# Revit family: Washfountain_Lavatory-Bradley_Corp-WF2808-Type_O_Drain
name_source: partatom
category: Plumbing Fixtures
revit_build: Autodesk Revit MEP 2012 (Build: 20110309_2315(x64)
units: mm (PartAtom-declared; Revit-internal decimal feet)

## types (1)
- Washfountain_Lavatory-Bradley_Corp-WF2808-Type_O_Drain
    ADA Compliant = Yes
    Assembly Code = D2010300
    Buy American Act = No
    CWFU = 0
    Cold Lavatory Inlet = 1/2"
    Cold Lavatory Inlet Radius = 1/4"
    Description = Washfountain, 54" Circular with 9" Deep Bowl
    Drain = 2"
    Drain Radius = 1"
    Flow Rate = 5.0 gal/min
    Frequency = 50 Hz
    HWFU = 0
    Hot Lavatory Inlet = 1/2"
    Hot Lavatory Inlet Radius = 1/4"
    Industry Standards = ANSI Z124.3, Z124.6 and ANSI/ICPA SS-1-2001
    Manufacturer = Bradley Corp
    MasterFormat Number = 22 42 16
    MasterFormat Title = Commercial Lavatories and Sinks
    Material Note = Other Terrazzo colors available - See www.bradleycorp.com
    Model = WF2808
    OmniClass Table 21 Number = 21-04 20 10 60
    OmniClass Table 21 Title = Plumbing Fixtures
    OmniClass Table 23 Number = 23-31 13 00
    OmniClass Table 23 Title = Sinks/Lavatories
    Operating Water Pressure Range = 20 - 80 PSI
    Pedestal Height = 26 "
    Pedestal Material = Plastic - Bradley Corp - Black
    Product Tech Data URL - English = http://bradleycorp.com
    Rim Height = 29 "
    Sensor Module Height = 40.75 "
    Specifications URL = http://www.bradleycorp.com
    Spray Head Height = 37.25 "
    URL = http://www.bradleycorp.com
    Version = 2.0
    Voltage = 110 V
    WFU = 0
    Width = 54 "

## geometry (parser evidence)
native form markers: Blend x14
no freeform markers — native parametric forms only
